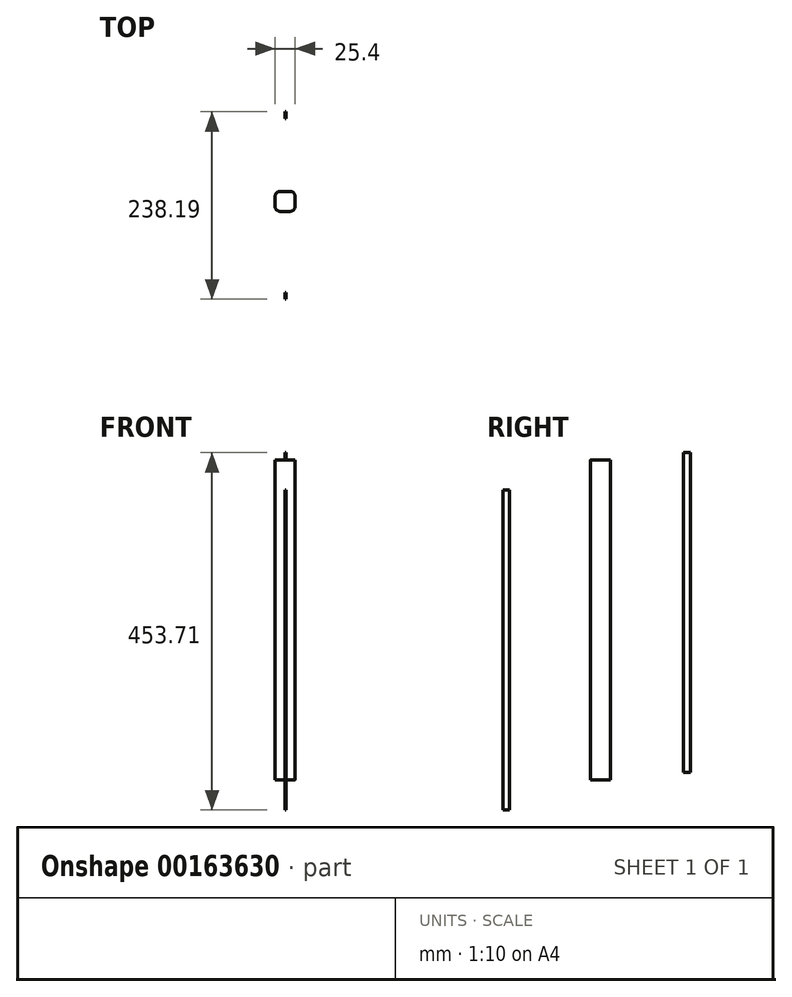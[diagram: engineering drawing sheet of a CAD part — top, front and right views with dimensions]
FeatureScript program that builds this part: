
annotation { "Feature Type Name" : "Feature", "Feature Type Description" : "" }
export const myFeature = defineFeature(function(context is Context, id is Id, definition is map)
    precondition{}
    {
        {
            var Q0;
            Q0=qCreatedBy(makeId("Top.planeOp"),FACE);
            var sketch = newSketch(context, id + "F0", { "sketchPlane" : qUnion([Q0])});
            skLineSegment(sketch, "E0.bottom", {"start": v(6.35, 12.7) * mm, "end": v(-6.35, 12.7) * mm});
            skLineSegment(sketch, "E0.top", {"start": v(6.35, -12.7) * mm, "end": v(-6.35, -12.7) * mm});
            skLineSegment(sketch, "E0.left", {"start": v(12.7, 6.35) * mm, "end": v(12.7, -6.35) * mm});
            skLineSegment(sketch, "E0.right", {"start": v(-12.7, 6.35) * mm, "end": v(-12.7, -6.35) * mm});
            skPoint(sketch, "E0.middle", {"position": v(0, 0) * mm});
            skPoint(sketch, "E1.visualSharp", {"position": v(-12.7, 12.7) * mm});
            skArc(sketch, "E1.filletArc", {"start": v(-6.35, 12.7) * mm, "mid": v(-10.84, 10.84) * mm, "end": v(-12.7, 6.35) * mm});
            skPoint(sketch, "E2.visualSharp", {"position": v(-12.7, -12.7) * mm});
            skArc(sketch, "E2.filletArc", {"start": v(-12.7, -6.35) * mm, "mid": v(-10.84, -10.84) * mm, "end": v(-6.35, -12.7) * mm});
            skPoint(sketch, "E3.visualSharp", {"position": v(12.7, -12.7) * mm});
            skArc(sketch, "E3.filletArc", {"start": v(6.35, -12.7) * mm, "mid": v(10.84, -10.84) * mm, "end": v(12.7, -6.35) * mm});
            skPoint(sketch, "E4.visualSharp", {"position": v(12.7, 12.7) * mm});
            skArc(sketch, "E4.filletArc", {"start": v(12.7, 6.35) * mm, "mid": v(10.84, 10.84) * mm, "end": v(6.35, 12.7) * mm});
            skSolve(sketch);
        }
        {
            var Q0;
            Q0=qSketchRegion(id+"F0",true);
            extrude(context, id + "F1", {"entities" : qUnion([Q0]), "depth" : 406.4 * mm});
        }
        {
            var Q0;
            Q0=qCreatedBy(makeId("Right.planeOp"),FACE);
            var sketch = newSketch(context, id + "F2", { "sketchPlane" : qUnion([Q0])});
            skLineSegment(sketch, "E5.bottom", {"start": v(-124.27, 368.3) * mm, "end": v(-115.8, 368.3) * mm});
            skLineSegment(sketch, "E5.top", {"start": v(-124.27, -38.1) * mm, "end": v(-115.8, -38.1) * mm});
            skLineSegment(sketch, "E5.left", {"start": v(-124.27, 368.3) * mm, "end": v(-124.27, -38.1) * mm});
            skLineSegment(sketch, "E5.right", {"start": v(-115.8, 368.3) * mm, "end": v(-115.8, -38.1) * mm});
            skSolve(sketch);
        }
        {
            var Q0;
            Q0=makeQuery(id+"F2.imprint","IMPRINT",FACE,{"disambiguationData":[TD([[makeQuery(id+"F2.imprint","IMPRINT",EDGE,{"derivedFrom":sQuery(id+"F2.wireOp",EDGE,"E5.bottom")}),-1.0]])]});
            extrude(context, id + "F3", {"entities" : qUnion([Q0]), "depth" : 1.27 * mm});
        }
        {
            var Q0;
            Q0=qCreatedBy(makeId("Right.planeOp"),FACE);
            var sketch = newSketch(context, id + "F4", { "sketchPlane" : qUnion([Q0])});
            skLineSegment(sketch, "E6.bottom", {"start": v(105.46, 415.6) * mm, "end": v(113.92, 415.6) * mm});
            skLineSegment(sketch, "E6.top", {"start": v(105.46, 9.2) * mm, "end": v(113.92, 9.2) * mm});
            skLineSegment(sketch, "E6.left", {"start": v(105.46, 415.6) * mm, "end": v(105.46, 9.2) * mm});
            skLineSegment(sketch, "E6.right", {"start": v(113.92, 415.6) * mm, "end": v(113.92, 9.2) * mm});
            skSolve(sketch);
        }
        {
            var Q0;
            Q0=makeQuery(id+"F4.imprint","IMPRINT",FACE,{"disambiguationData":[TD([[makeQuery(id+"F4.imprint","IMPRINT",EDGE,{"derivedFrom":sQuery(id+"F4.wireOp",EDGE,"E6.bottom")}),-1.0]])]});
            extrude(context, id + "F5", {"entities" : qUnion([Q0]), "depth" : 1.27 * mm});
        }
    });
